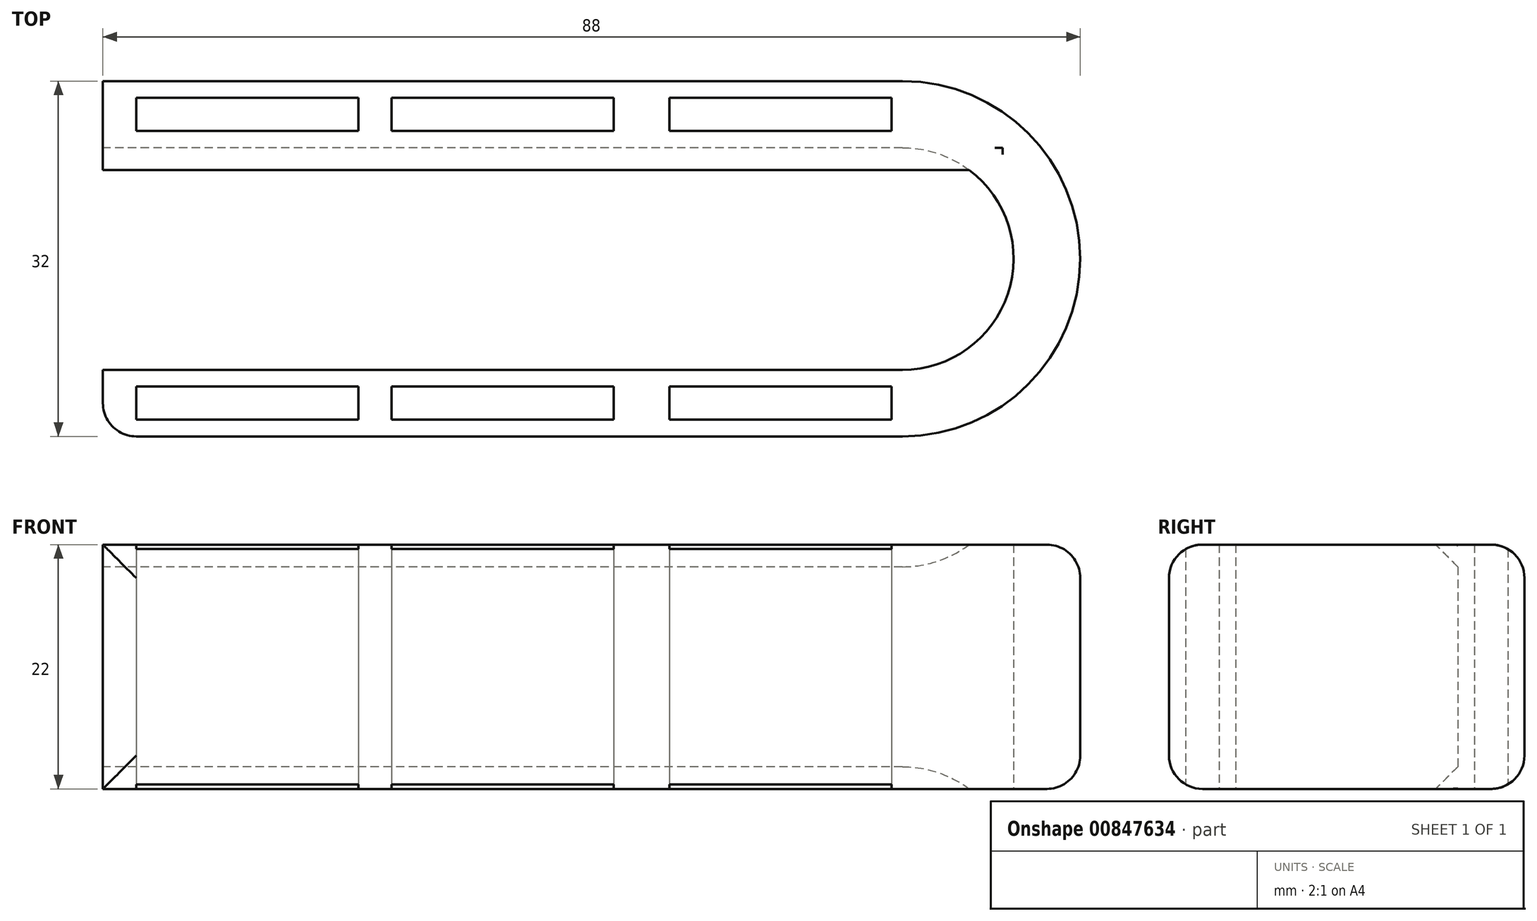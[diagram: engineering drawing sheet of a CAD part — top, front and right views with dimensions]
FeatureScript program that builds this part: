
annotation { "Feature Type Name" : "Feature", "Feature Type Description" : "" }
export const myFeature = defineFeature(function(context is Context, id is Id, definition is map)
    precondition{}
    {
        {
            var Q0;
            Q0=qCreatedBy(makeId("Top.planeOp"),FACE);
            var sketch = newSketch(context, id + "F0", { "sketchPlane" : qUnion([Q0])});
            skLineSegment(sketch, "E0.bottom", {"start": v(-36, -3) * mm, "end": v(36, -3) * mm});
            skLineSegment(sketch, "E0.top", {"start": v(-36, 3) * mm, "end": v(36, 3) * mm});
            skLineSegment(sketch, "E0.left", {"start": v(-36, -3) * mm, "end": v(-36, 3) * mm});
            skLineSegment(sketch, "E0.right", {"start": v(36, -3) * mm, "end": v(36, 3) * mm});
            skPoint(sketch, "E0.middle", {"position": v(0, 0) * mm});
            skLineSegment(sketch, "E1.bottom", {"start": v(-36, 23) * mm, "end": v(36, 23) * mm});
            skLineSegment(sketch, "E1.top", {"start": v(-36, 29) * mm, "end": v(36, 29) * mm});
            skLineSegment(sketch, "E1.left", {"start": v(-36, 23) * mm, "end": v(-36, 29) * mm});
            skLineSegment(sketch, "E1.right", {"start": v(36, 23) * mm, "end": v(36, 29) * mm});
            skPoint(sketch, "E1.middle", {"position": v(0, 26) * mm});
            skArc(sketch, "E2", {"start": v(36, 29) * mm, "mid": v(52, 13) * mm, "end": v(36, -3) * mm});
            skArc(sketch, "E3", {"start": v(36, 23) * mm, "mid": v(46, 13) * mm, "end": v(36, 3) * mm});
            skArc(sketch, "E4", {"start": v(36, 3) * mm, "mid": v(43.07, 5.93) * mm, "end": v(46, 13) * mm});
            skLineSegment(sketch, "E5.bottom", {"start": v(-9.94, 23) * mm, "end": v(9.94, 23) * mm});
            skLineSegment(sketch, "E5.top", {"start": v(-9.94, 29) * mm, "end": v(9.94, 29) * mm});
            skLineSegment(sketch, "E6.bottom", {"start": v(-10.8, -3) * mm, "end": v(10.8, -3) * mm});
            skLineSegment(sketch, "E6.top", {"start": v(-10.8, 3) * mm, "end": v(10.8, 3) * mm});
            skLineSegment(sketch, "E7.bottom", {"start": v(19.37, 23) * mm, "end": v(32.3, 23) * mm});
            skLineSegment(sketch, "E7.top", {"start": v(17.7, 29) * mm, "end": v(30.63, 29) * mm});
            skPoint(sketch, "E7.middle", {"position": v(25, 26) * mm});
            skLineSegment(sketch, "E8.bottom", {"start": v(18.1, -3) * mm, "end": v(28.97, -3) * mm});
            skLineSegment(sketch, "E8.top", {"start": v(21.03, 3) * mm, "end": v(31.9, 3) * mm});
            skPoint(sketch, "E8.middle", {"position": v(25, 0) * mm});
            skLineSegment(sketch, "E9.bottom", {"start": v(-29.18, -3) * mm, "end": v(-14.3, -3) * mm});
            skLineSegment(sketch, "E9.top", {"start": v(-31.7, 3) * mm, "end": v(-16.82, 3) * mm});
            skPoint(sketch, "E9.middle", {"position": v(-23, 0) * mm});
            skLineSegment(sketch, "E10.bottom", {"start": v(-29.27, 23) * mm, "end": v(-15, 23) * mm});
            skLineSegment(sketch, "E10.top", {"start": v(-31, 29) * mm, "end": v(-16.73, 29) * mm});
            skPoint(sketch, "E10.middle", {"position": v(-23, 26) * mm});
            skLineSegment(sketch, "E11.bottom", {"start": v(-33, 24.5) * mm, "end": v(-13, 24.5) * mm});
            skLineSegment(sketch, "E11.top", {"start": v(-33, 27.5) * mm, "end": v(-13, 27.5) * mm});
            skLineSegment(sketch, "E11.left", {"start": v(-33, 24.5) * mm, "end": v(-33, 27.5) * mm});
            skLineSegment(sketch, "E11.right", {"start": v(-13, 24.5) * mm, "end": v(-13, 27.5) * mm});
            skLineSegment(sketch, "E12.bottom", {"start": v(-10, 24.5) * mm, "end": v(10, 24.5) * mm});
            skLineSegment(sketch, "E12.top", {"start": v(-10, 27.5) * mm, "end": v(10, 27.5) * mm});
            skLineSegment(sketch, "E12.left", {"start": v(-10, 24.5) * mm, "end": v(-10, 27.5) * mm});
            skLineSegment(sketch, "E12.right", {"start": v(10, 24.5) * mm, "end": v(10, 27.5) * mm});
            skLineSegment(sketch, "E13.bottom", {"start": v(15, 24.5) * mm, "end": v(35, 24.5) * mm});
            skLineSegment(sketch, "E13.top", {"start": v(15, 27.5) * mm, "end": v(35, 27.5) * mm});
            skLineSegment(sketch, "E13.left", {"start": v(15, 24.5) * mm, "end": v(15, 27.5) * mm});
            skLineSegment(sketch, "E13.right", {"start": v(35, 24.5) * mm, "end": v(35, 27.5) * mm});
            skLineSegment(sketch, "E14.bottom", {"start": v(15, -1.5) * mm, "end": v(35, -1.5) * mm});
            skLineSegment(sketch, "E14.top", {"start": v(15, 1.5) * mm, "end": v(35, 1.5) * mm});
            skLineSegment(sketch, "E14.left", {"start": v(15, -1.5) * mm, "end": v(15, 1.5) * mm});
            skLineSegment(sketch, "E14.right", {"start": v(35, -1.5) * mm, "end": v(35, 1.5) * mm});
            skLineSegment(sketch, "E15.bottom", {"start": v(-10, -1.5) * mm, "end": v(10, -1.5) * mm});
            skLineSegment(sketch, "E15.top", {"start": v(-10, 1.5) * mm, "end": v(10, 1.5) * mm});
            skLineSegment(sketch, "E15.left", {"start": v(-10, -1.5) * mm, "end": v(-10, 1.5) * mm});
            skLineSegment(sketch, "E15.right", {"start": v(10, -1.5) * mm, "end": v(10, 1.5) * mm});
            skLineSegment(sketch, "E16.bottom", {"start": v(-33, -1.5) * mm, "end": v(-13, -1.5) * mm});
            skLineSegment(sketch, "E16.top", {"start": v(-33, 1.5) * mm, "end": v(-13, 1.5) * mm});
            skLineSegment(sketch, "E16.left", {"start": v(-33, -1.5) * mm, "end": v(-33, 1.5) * mm});
            skLineSegment(sketch, "E16.right", {"start": v(-13, -1.5) * mm, "end": v(-13, 1.5) * mm});
            skSolve(sketch);
        }
        {
            var Q0;
            Q0=makeQuery(id+"F0.imprint","IMPRINT",FACE,{"disambiguationData":[TD([[makeQuery(id+"F0.imprint","IMPRINT",EDGE,{"derivedFrom":sQuery(id+"F0.wireOp",EDGE,"E0.right")}),-1.0]])]});
            var Q1;
            {var subQ8=sQuery(id+"F0.wireOp",EDGE,"E1.left");Q1=makeQuery(id+"F0.imprint","IMPRINT",FACE,{"disambiguationData":[TD([[makeQuery(id+"F0.imprint","IMPRINT",EDGE,{"derivedFrom":subQ8}),-1.0]])]});}
            var Q2;
            {var subQ6=sQuery(id+"F0.wireOp",EDGE,"E0.left");Q2=makeQuery(id+"F0.imprint","IMPRINT",FACE,{"disambiguationData":[TD([[makeQuery(id+"F0.imprint","IMPRINT",EDGE,{"derivedFrom":subQ6}),-1.0]])]});}
            extrude(context, id + "F1", {"entities" : qUnion([Q0, Q1, Q2]), "depth" : 22 * mm, "offsetDistance" : 25 * mm});
        }
        {
            var Q0;
            Q0=makeQuery(id+"F1.opExtrude","SWEPT_FACE",FACE,{"disambiguationData":[OSD([sQuery(id+"F0.wireOp",EDGE,"E1.bottom"),sQuery(id+"F0.wireOp",EDGE,"E5.bottom"),sQuery(id+"F0.wireOp",EDGE,"E7.bottom"),sQuery(id+"F0.wireOp",EDGE,"E10.bottom")])]});
            var sketch = newSketch(context, id + "F2", { "sketchPlane" : qUnion([Q0])});
            skLineSegment(sketch, "E17.bottom", {"start": v(36, 22) * mm, "end": v(-36, 22) * mm});
            skLineSegment(sketch, "E17.top", {"start": v(36, 20) * mm, "end": v(-36, 20) * mm});
            skLineSegment(sketch, "E17.left", {"start": v(36, 22) * mm, "end": v(36, 20) * mm});
            skLineSegment(sketch, "E17.right", {"start": v(-36, 22) * mm, "end": v(-36, 20) * mm});
            skLineSegment(sketch, "E18.bottom", {"start": v(36, 0) * mm, "end": v(-36, 0) * mm});
            skLineSegment(sketch, "E18.top", {"start": v(36, 2) * mm, "end": v(-36, 2) * mm});
            skLineSegment(sketch, "E18.left", {"start": v(36, 0) * mm, "end": v(36, 2) * mm});
            skLineSegment(sketch, "E18.right", {"start": v(-36, 0) * mm, "end": v(-36, 2) * mm});
            skLineSegment(sketch, "E19.bottom", {"start": v(36, 2) * mm, "end": v(45, 2) * mm});
            skLineSegment(sketch, "E19.top", {"start": v(36, 0) * mm, "end": v(45, 0) * mm});
            skLineSegment(sketch, "E19.left", {"start": v(36, 2) * mm, "end": v(36, 0) * mm});
            skLineSegment(sketch, "E19.right", {"start": v(45, 2) * mm, "end": v(45, 0) * mm});
            skLineSegment(sketch, "E20.bottom", {"start": v(36, 20) * mm, "end": v(45, 20) * mm});
            skLineSegment(sketch, "E20.top", {"start": v(36, 22) * mm, "end": v(45, 22) * mm});
            skLineSegment(sketch, "E20.left", {"start": v(36, 20) * mm, "end": v(36, 22) * mm});
            skLineSegment(sketch, "E20.right", {"start": v(45, 20) * mm, "end": v(45, 22) * mm});
            skSolve(sketch);
        }
        {
            var Q0;
            Q0=makeQuery(id+"F2.imprint","IMPRINT",FACE,{"disambiguationData":[TD([[makeQuery(id+"F2.imprint","IMPRINT",EDGE,{"derivedFrom":sQuery(id+"F2.wireOp",EDGE,"E17.bottom")}),-1.0]])]});
            var Q1;
            Q1=makeQuery(id+"F2.imprint","IMPRINT",FACE,{"disambiguationData":[TD([[makeQuery(id+"F2.imprint","IMPRINT",EDGE,{"derivedFrom":sQuery(id+"F2.wireOp",EDGE,"E18.bottom")}),1.0]])]});
            extrude(context, id + "F3", {"entities" : qUnion([Q0, Q1]), "operationType" : NewBodyOperationType.ADD, "depth" : 2 * mm, "offsetDistance" : 25 * mm});
        }
        {
            var Q0;
            Q0=makeQuery(id+"F3.opExtrude","CAP_EDGE",EDGE,{"disambiguationData":[OSD([sQuery(id+"F2.wireOp",EDGE,"E17.top")])],"isStart":false});
            fillet(context, id + "F4", {"entities" : qUnion([Q0]), "radius" : 2 * mm, "tangentPropagation" : true, "allowEdgeOverflow" : false});
        }
        {
            var Q0;
            Q0=makeQuery(id+"F3.opExtrude","CAP_EDGE",EDGE,{"disambiguationData":[OSD([sQuery(id+"F2.wireOp",EDGE,"E18.top")])],"isStart":false});
            fillet(context, id + "F5", {"entities" : qUnion([Q0]), "radius" : 2 * mm, "tangentPropagation" : true, "allowEdgeOverflow" : false});
        }
        {
            var Q0;
            Q0=makeQuery(id+"F1.opExtrude","SWEPT_FACE",FACE,{"disambiguationData":[OSD([sQuery(id+"F0.wireOp",EDGE,"E0.bottom"),sQuery(id+"F0.wireOp",EDGE,"E6.bottom"),sQuery(id+"F0.wireOp",EDGE,"E8.bottom"),sQuery(id+"F0.wireOp",EDGE,"E9.bottom")])]});
            fillet(context, id + "F6", {"entities" : qUnion([Q0]), "radius" : 3 * mm, "tangentPropagation" : true, "allowEdgeOverflow" : false});
        }
        {
            var Q0;
            Q0 = qSketchRegion(id + "F2", true);
            extrude(context, id + "F7", {"entities" : qUnion([Q0]), "operationType" : NewBodyOperationType.ADD, "depth" : 4 * mm, "offsetDistance" : 25 * mm});
        }
        {
            var Q0;
            Q0=makeQuery(id+"F7.opExtrude","CAP_EDGE",EDGE,{"disambiguationData":[OSD([sQuery(id+"F2.wireOp",EDGE,"E17.top"),sQuery(id+"F2.wireOp",EDGE,"E20.bottom")])],"isStart":false});
            var Q1;
            Q1=makeQuery(id+"F7.opExtrude","CAP_EDGE",EDGE,{"disambiguationData":[OSD([sQuery(id+"F2.wireOp",EDGE,"E18.top"),sQuery(id+"F2.wireOp",EDGE,"E19.bottom")])],"isStart":false});
            chamfer(context, id + "F8", {"entities" : qUnion([Q0, Q1]), "width" : 4 * mm, "tangentPropagation" : true});
        }
    });
